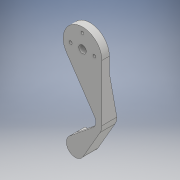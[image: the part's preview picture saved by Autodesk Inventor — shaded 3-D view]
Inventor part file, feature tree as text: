
AUTODESK INVENTOR PART (.ipt)
format: ipt  version: 2017 (Build 210142000, 142)  size: 254,464 bytes
history: native  units: mm
features: sketch x4, extrude x3, hole x2, fillet x2
ambient origin geometry x8: Origin, YZ Plane, XZ Plane, XY Plane, X Axis, Y Axis, Z Axis, Center Point
bodies: Solid1 (feature_tree)
feature tree (11):
  extrude  "Extrusion1"  Depth=13.0mm
  extrude  "Extrusion2"  Depth=5.0mm
  extrude  "Extrusion4"  Depth=23.0mm
  hole  "Hole1"  [1 undecoded]
  fillet  "Fillet1"  Radius=3.0mm
  fillet  "Fillet2"  Radius=13.0mm
  hole  "Hole4"  [1 undecoded]
  sketch  "Sketch1"  dims[d0=38.0mm d2=13.0mm]
  sketch  "Sketch3"  dims[d4=9.0mm d7=5.0mm]
  sketch  "Sketch5"  dims[d8=30.0deg d9=23.0mm]
  sketch  "Sketch6"  dims[d10=6.0mm d11=4.0mm d12=3.0mm d13=0.0mm d22=13.0mm d23=26.0mm d25=5.0mm d29=7.0mm d30=0.0mm d34=5.0mm d35=60.0mm d36=28.0mm d37=26.0mm d38=0.0mm d39=19.0mm d40=19.0mm d41=9.5mm d42=9.5mm d43=2.0mm d44=6.0mm d45=4.0mm d46=2.5mm d47=90.0deg d48=8.0mm d49=20.594885mm d52=4.0mm d62=2.0mm d63=2.0mm d98=10.0mm d99=10.0mm d86=5.0mm d87=6.0mm d88=4.0mm d89=2.0mm d90=90.0deg d91=8.0mm d92=20.594885mm d94=6.5mm d95=8.0mm d96=16.0mm d97=8.0mm d78=1.0mm d79=1.0mm]
note: 2 required parameter values undecoded (feature->parameter linkage not recoverable at this tier; creation-order binding heuristic only, values carry confidence <= 0.55)
